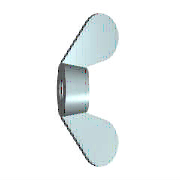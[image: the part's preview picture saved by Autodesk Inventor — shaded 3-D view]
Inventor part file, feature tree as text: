
AUTODESK INVENTOR PART (.ipt)
format: ipt  version: 2020 (Build 240168000, 168)  size: 171,520 bytes
history: native  units: mm (DEFAULTED — no unit token found)
features: sketch x2, extrude x1, mirror x1, hole x1, other x1, plane x1
ambient origin geometry x7: Origin, YZ Plane, XZ Plane, X Axis, Y Axis, Z Axis, Center Point
bodies: Solid1 (feature_tree), Body (feature_tree)
feature tree (7):
  sketch  "Sketch1"  dims[d0=7.0mm d1=7.5mm]
  extrude  "Wing1"  Depth=7.5mm
  mirror  "Wing2"
  hole  "Thread"  [1 undecoded]
  other  "Work Axis1"
  plane  "Work Plane1"
  sketch  "Sketch2"  dims[d2=7.0mm d3=3.0mm d57=90.0deg d4=4.6mm d5=8.0mm d6=1.9mm d7=0.0mm d8=0.633333mm d97=3.242mm d98=6.0mm d99=4.0mm d100=2.0mm d101=14.3117mm d102=8.0mm d103=20.594885mm d9=0.378886mm d10=30.0deg d11=0.0mm d108=0.0mm d109=0.378886mm d110=0.0mm d111=0.0mm d112=0.0mm]
note: 1 required parameter value undecoded (feature->parameter linkage not recoverable at this tier; creation-order binding heuristic only, values carry confidence <= 0.55)
